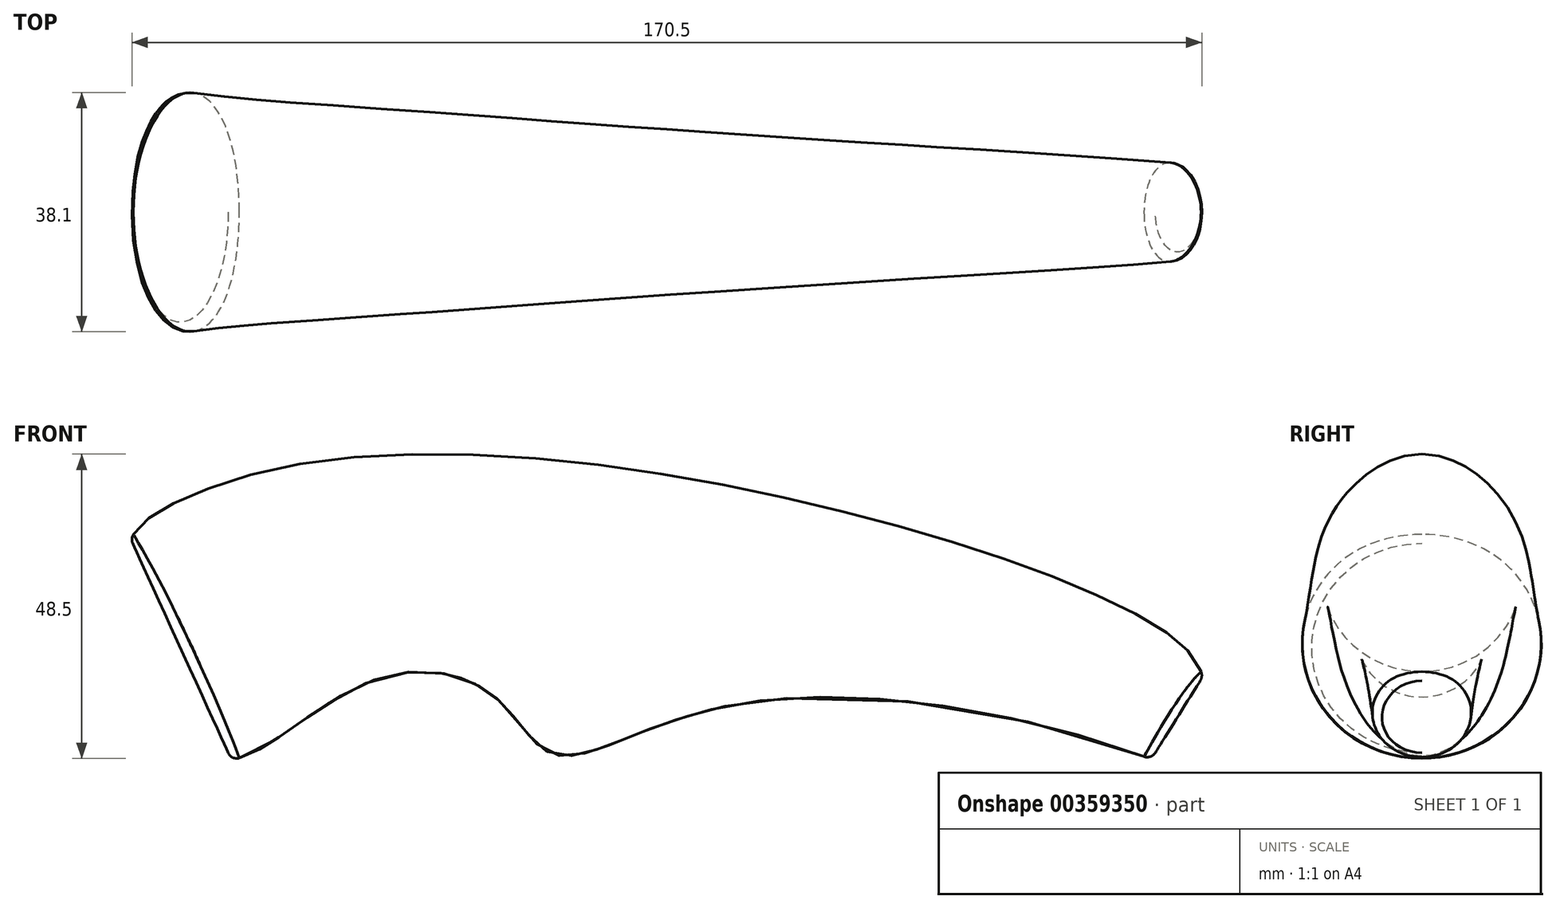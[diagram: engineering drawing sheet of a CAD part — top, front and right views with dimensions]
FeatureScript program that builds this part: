
annotation { "Feature Type Name" : "Feature", "Feature Type Description" : "" }
export const myFeature = defineFeature(function(context is Context, id is Id, definition is map)
    precondition{}
    {
        {
            var Q0;
            Q0=qCreatedBy(makeId("Front.planeOp"),FACE);
            var sketch = newSketch(context, id + "F0", { "sketchPlane" : qUnion([Q0])});
            skLineSegment(sketch, "E0", {"start": v(-16, 35.1) * mm, "end": v(0, 0) * mm});
            skLineSegment(sketch, "E1", {"start": v(146.62, 0) * mm, "end": v(154.86, 13.2) * mm});
            skFitSpline(sketch, "E2", {"points": [v(-16, 35.1) * mm, v(-11.17, 39.7) * mm, v(8.44, 46.57) * mm, v(49.9, 47.84) * mm, v(96.12, 39.8) * mm, v(131.2, 29) * mm, v(149.89, 19.62) * mm, v(154.86, 13.2) * mm], "startDerivative": vector(36.13, 75.18) * mm, "endDerivative": vector(39.03, -101.51) * mm});
            skFitSpline(sketch, "E3", {"points": [v(0, 0) * mm, v(21.93, 12.33) * mm, v(41.79, 10.16) * mm, v(50.7, 1.03) * mm, v(62.02, 2.95) * mm, v(84.73, 9.4) * mm, v(146.62, 0) * mm], "startDerivative": vector(83.75, 0) * mm, "endDerivative": vector(248.73, -93.3) * mm});
            skSolve(sketch);
        }
        {
            var Q0;
            Q0=sQuery(id+"F0.wireOp",EDGE,"E1");
            cPlane(context, id + "F1", {"entities" : qUnion([Q0]), "cplaneType" : CPlaneType.LINE_ANGLE, "offset" : 25.4 * mm, "angle" : 0 * degree, "width" : 152.4 * mm, "height" : 152.4 * mm});
        }
        {
            var Q0;
            Q0=qCreatedBy(id+"F1.planeOp",FACE);
            var sketch = newSketch(context, id + "F2", { "sketchPlane" : qUnion([Q0])});
            skPoint(sketch, "E4.0", {"position": v(0, 85.48) * mm});
            skCircle(sketch, "E5", {"center": v(0, 85.48) * mm, "radius": 7.78 * mm});
            skPoint(sketch, "E6.0", {"position": v(0, 93.26) * mm});
            skSolve(sketch);
        }
        {
            var Q0;
            Q0=sQuery(id+"F0.wireOp",EDGE,"E0");
            cPlane(context, id + "F3", {"entities" : qUnion([Q0]), "cplaneType" : CPlaneType.LINE_ANGLE, "offset" : 25.4 * mm, "angle" : 0 * degree, "width" : 152.4 * mm, "height" : 152.4 * mm});
        }
        {
            var Q0;
            Q0=qCreatedBy(id+"F3.planeOp",FACE);
            var sketch = newSketch(context, id + "F4", { "sketchPlane" : qUnion([Q0])});
            skPoint(sketch, "E7.0", {"position": v(0, 38.57) * mm});
            skPoint(sketch, "E7.1", {"position": v(0, 19.29) * mm});
            skCircle(sketch, "E8", {"center": v(0, 19.29) * mm, "radius": 19.29 * mm});
            skSolve(sketch);
        }
        {
            var Q0;
            Q0=makeQuery(id+"F2.imprint","IMPRINT",FACE,{"disambiguationData":[TD([[makeQuery(id+"F2.imprint","IMPRINT",EDGE,{"derivedFrom":sQuery(id+"F2.wireOp",EDGE,"E5")}),1.0]])]});
            var Q1;
            Q1=makeQuery(id+"F4.imprint","IMPRINT",FACE,{"disambiguationData":[TD([[makeQuery(id+"F4.imprint","IMPRINT",EDGE,{"derivedFrom":sQuery(id+"F4.wireOp",EDGE,"E8")}),1.0]])]});
            var Q2;
            Q2=sQuery(id+"F2.wireOp",EDGE,"E5");
            var Q3;
            Q3=sQuery(id+"F4.wireOp",EDGE,"E8");
            var Q4;
            Q4=sQuery(id+"F0.wireOp",EDGE,"E2");
            var Q5;
            Q5=sQuery(id+"F0.wireOp",EDGE,"E3");
            loft(context, id + "F5", {"addGuides" : true, "sheetProfilesArray" : [{ "sheetProfileEntities" : qUnion([Q0]) }, { "sheetProfileEntities" : qUnion([Q1]) }], "wireProfilesArray" : [{ "wireProfileEntities" : qUnion([Q2]) }, { "wireProfileEntities" : qUnion([Q3]) }], "guidesArray" : [{ "guideEntities" : qUnion([Q4]), "guideDerivativeType" : LoftGuideDerivativeType.DEFAULT, "guideDerivativeMagnitude" : 1 }, { "guideEntities" : qUnion([Q5]), "guideDerivativeType" : LoftGuideDerivativeType.DEFAULT, "guideDerivativeMagnitude" : 1 }]});
        }
        {
            var Q0;
            Q0=makeQuery(id+"F5.opLoft","MID_CAP_EDGE",EDGE,{"disambiguationData":[OSD([sQuery(id+"F0.wireOp",EDGE,"E2"),sQuery(id+"F0.wireOp",EDGE,"E3"),sQuery(id+"F4.wireOp",EDGE,"E8")]),OD(0.0)],"capPos":1.0});
            var Q1;
            Q1=makeQuery(id+"F5.opLoft","MID_CAP_EDGE",EDGE,{"disambiguationData":[OSD([sQuery(id+"F0.wireOp",EDGE,"E2"),sQuery(id+"F0.wireOp",EDGE,"E3"),sQuery(id+"F2.wireOp",EDGE,"E5")]),OD(0.0)],"capPos":0.0});
            fillet(context, id + "F6", {"entities" : qUnion([Q0, Q1]), "radius" : 1.52 * mm, "tangentPropagation" : true, "allowEdgeOverflow" : false});
        }
    });
